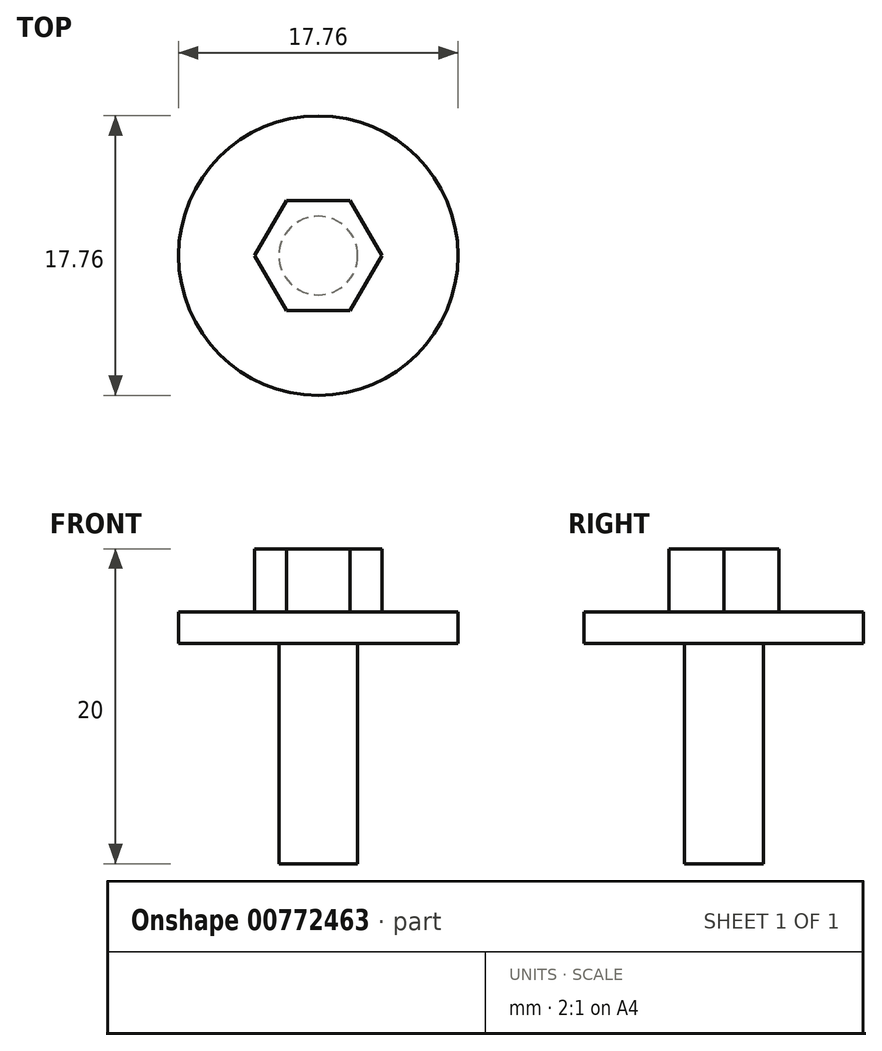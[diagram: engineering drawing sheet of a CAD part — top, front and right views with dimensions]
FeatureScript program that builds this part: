
annotation { "Feature Type Name" : "Feature", "Feature Type Description" : "" }
export const myFeature = defineFeature(function(context is Context, id is Id, definition is map)
    precondition{}
    {
        {
            var Q0;
            Q0=qCreatedBy(makeId("Top.planeOp"),FACE);
            var sketch = newSketch(context, id + "F0", { "sketchPlane" : qUnion([Q0])});
            skCircle(sketch, "E0", {"center": v(0, 0) * mm, "radius": 8.88 * mm});
            skSolve(sketch);
        }
        {
            var Q0;
            Q0=makeQuery(id+"F0.imprint","IMPRINT",FACE,{"disambiguationData":[TD([[makeQuery(id+"F0.imprint","IMPRINT",EDGE,{"derivedFrom":sQuery(id+"F0.wireOp",EDGE,"E0")}),1.0]])]});
            extrude(context, id + "F1", {"entities" : qUnion([Q0]), "depth" : 2 * mm, "offsetDistance" : 25 * mm});
        }
        {
            var Q0;
            Q0=makeQuery(id+"F1.opExtrude","CAP_FACE",FACE,{"disambiguationData":[OSD([sQuery(id+"F0.wireOp",EDGE,"E0")])],"isStart":true});
            var sketch = newSketch(context, id + "F2", { "sketchPlane" : qUnion([Q0])});
            skCircle(sketch, "E1", {"center": v(0, 0) * mm, "radius": 2.5 * mm});
            skSolve(sketch);
        }
        {
            var Q0;
            Q0=makeQuery(id+"F2.imprint","IMPRINT",FACE,{"disambiguationData":[TD([[makeQuery(id+"F2.imprint","IMPRINT",EDGE,{"derivedFrom":sQuery(id+"F2.wireOp",EDGE,"E1")}),1.0]])]});
            extrude(context, id + "F3", {"entities" : qUnion([Q0]), "operationType" : NewBodyOperationType.ADD, "depth" : 14 * mm, "offsetDistance" : 25 * mm});
        }
        {
            var Q0;
            Q0=makeQuery(id+"F1.opExtrude","CAP_FACE",FACE,{"disambiguationData":[OSD([sQuery(id+"F0.wireOp",EDGE,"E0")])],"isStart":false});
            var sketch = newSketch(context, id + "F4", { "sketchPlane" : qUnion([Q0])});
            skLineSegment(sketch, "E2", {"start": v(-2.02, -3.5) * mm, "end": v(2.02, -3.5) * mm});
            skLineSegment(sketch, "E3", {"start": v(2.02, -3.5) * mm, "end": v(4.04, 0) * mm});
            skLineSegment(sketch, "E4", {"start": v(4.04, 0) * mm, "end": v(2.02, 3.5) * mm});
            skLineSegment(sketch, "E5", {"start": v(2.02, 3.5) * mm, "end": v(-2.02, 3.5) * mm});
            skLineSegment(sketch, "E6", {"start": v(-2.02, 3.5) * mm, "end": v(-4.04, 0) * mm});
            skLineSegment(sketch, "E7", {"start": v(-4.04, 0) * mm, "end": v(-2.02, -3.5) * mm});
            skLineSegment(sketch, "E8", {"start": v(0, 0) * mm, "end": v(2.02, 3.5) * mm, "construction": true});
            skLineSegment(sketch, "E9", {"start": v(0, 0) * mm, "end": v(4.04, 0) * mm, "construction": true});
            skLineSegment(sketch, "E10", {"start": v(0, 0) * mm, "end": v(2.02, -3.5) * mm, "construction": true});
            skLineSegment(sketch, "E11", {"start": v(0, 0) * mm, "end": v(-2.02, 3.5) * mm, "construction": true});
            skLineSegment(sketch, "E12", {"start": v(0, 0) * mm, "end": v(-4.04, 0) * mm, "construction": true});
            skLineSegment(sketch, "E13", {"start": v(0, 0) * mm, "end": v(-2.02, -3.5) * mm, "construction": true});
            skSolve(sketch);
        }
        {
            var Q0;
            Q0=makeQuery(id+"F4.imprint","IMPRINT",FACE,{"disambiguationData":[TD([[makeQuery(id+"F4.imprint","IMPRINT",EDGE,{"derivedFrom":sQuery(id+"F4.wireOp",EDGE,"E2")}),1.0]])]});
            extrude(context, id + "F5", {"entities" : qUnion([Q0]), "operationType" : NewBodyOperationType.ADD, "depth" : 4 * mm, "offsetDistance" : 25 * mm});
        }
    });
